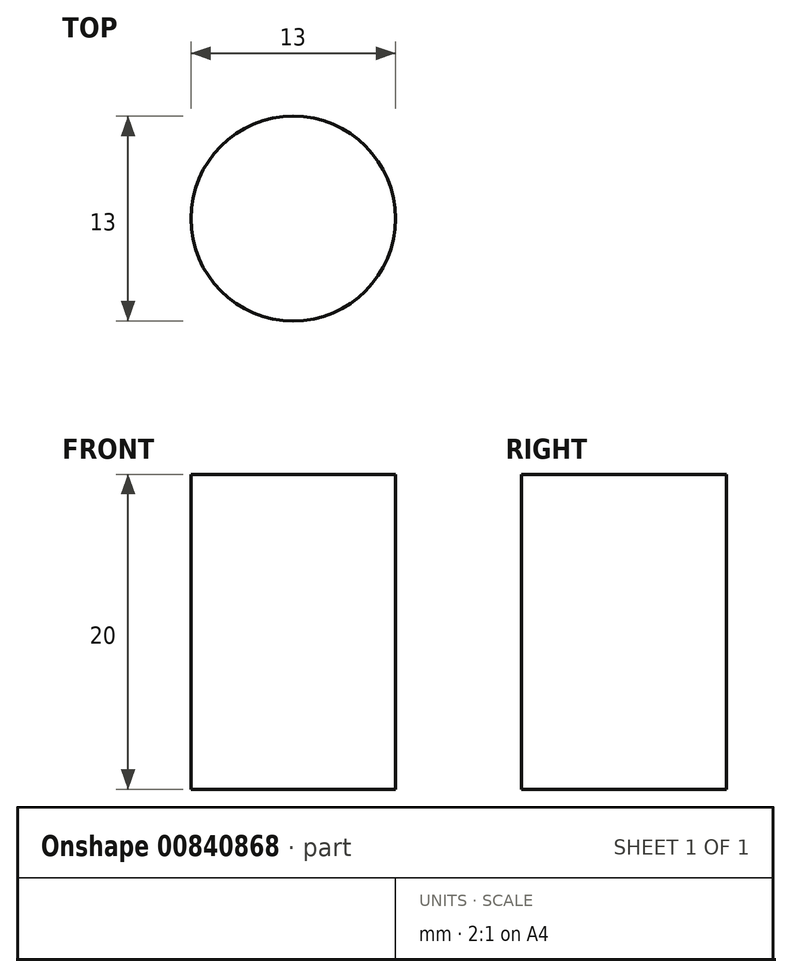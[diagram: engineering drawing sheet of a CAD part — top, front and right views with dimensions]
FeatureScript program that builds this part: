
annotation { "Feature Type Name" : "Feature", "Feature Type Description" : "" }
export const myFeature = defineFeature(function(context is Context, id is Id, definition is map)
    precondition{}
    {
        {
            var Q0;
            Q0=qCreatedBy(makeId("Front.planeOp"),FACE);
            var sketch = newSketch(context, id + "F0", { "sketchPlane" : qUnion([Q0])});
            skLineSegment(sketch, "E0.bottom", {"start": v(0, 0) * mm, "end": v(6.5, 0) * mm});
            skLineSegment(sketch, "E0.top", {"start": v(0, 20) * mm, "end": v(6.5, 20) * mm});
            skLineSegment(sketch, "E0.left", {"start": v(0, 0) * mm, "end": v(0, 20) * mm});
            skLineSegment(sketch, "E0.right", {"start": v(6.5, 0) * mm, "end": v(6.5, 20) * mm});
            skLineSegment(sketch, "E1", {"start": v(0, 0) * mm, "end": v(0, 29.37) * mm, "construction": true});
            skSolve(sketch);
        }
        {
            var Q0;
            Q0=qSketchRegion(id+"F0",true);
            var Q1;
            Q1=sQuery(id+"F0.wireOp",EDGE,"E1");
            revolve(context, id + "F1", {"surfaceOperationType" : NewSurfaceOperationType.NEW, "entities" : qUnion([Q0]), "axis" : qUnion([Q1]), "revolveType" : RevolveType.FULL});
        }
    });
